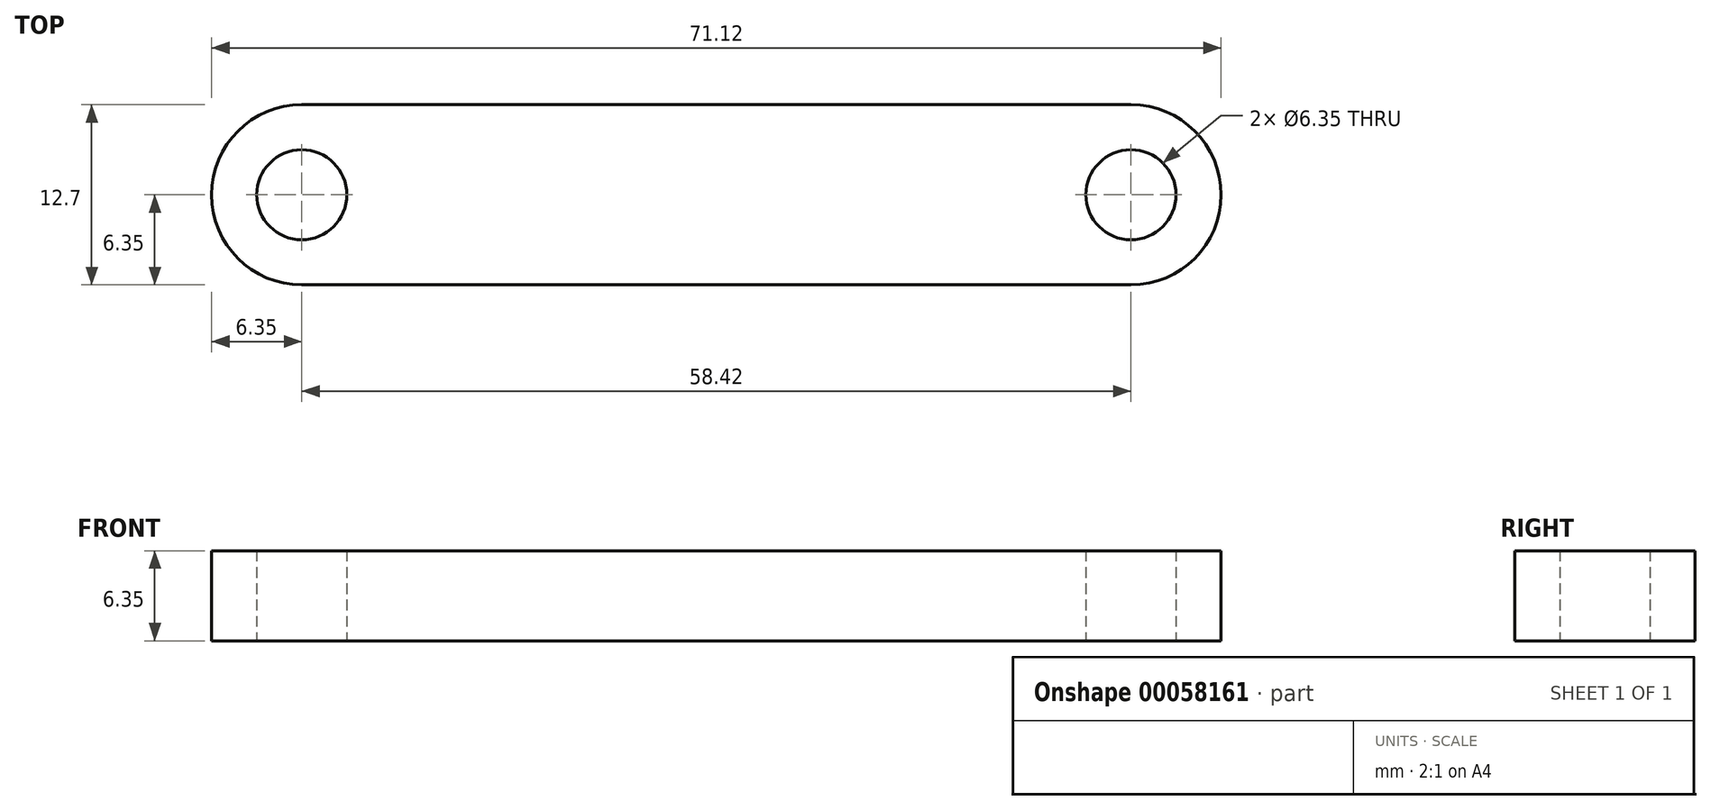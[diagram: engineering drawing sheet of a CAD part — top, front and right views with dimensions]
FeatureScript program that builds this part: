
annotation { "Feature Type Name" : "Feature", "Feature Type Description" : "" }
export const myFeature = defineFeature(function(context is Context, id is Id, definition is map)
    precondition{}
    {
        {
            var Q0;
            Q0=qCreatedBy(makeId("Top.planeOp"),FACE);
            var sketch = newSketch(context, id + "F0", { "sketchPlane" : qUnion([Q0])});
            skCircle(sketch, "E0", {"center": v(0, 0) * mm, "radius": 3.18 * mm});
            skArc(sketch, "E1", {"start": v(0, -6.35) * mm, "mid": v(6.35, 0) * mm, "end": v(0, 6.35) * mm});
            skCircle(sketch, "E2", {"center": v(-58.42, 0) * mm, "radius": 3.18 * mm});
            skArc(sketch, "E3", {"start": v(-58.42, 6.35) * mm, "mid": v(-64.77, 0) * mm, "end": v(-58.42, -6.35) * mm});
            skLineSegment(sketch, "E4", {"start": v(-58.42, 6.35) * mm, "end": v(0, 6.35) * mm});
            skLineSegment(sketch, "E5", {"start": v(-58.42, -6.35) * mm, "end": v(0, -6.35) * mm});
            skSolve(sketch);
        }
        {
            var Q0;
            Q0=makeQuery(id+"F0.imprint","IMPRINT",FACE,{"disambiguationData":[TD([[makeQuery(id+"F0.imprint","IMPRINT",EDGE,{"derivedFrom":sQuery(id+"F0.wireOp",EDGE,"E0")}),-1.0]])]});
            extrude(context, id + "F1", {"entities" : qUnion([Q0]), "depth" : 6.35 * mm});
        }
    });
